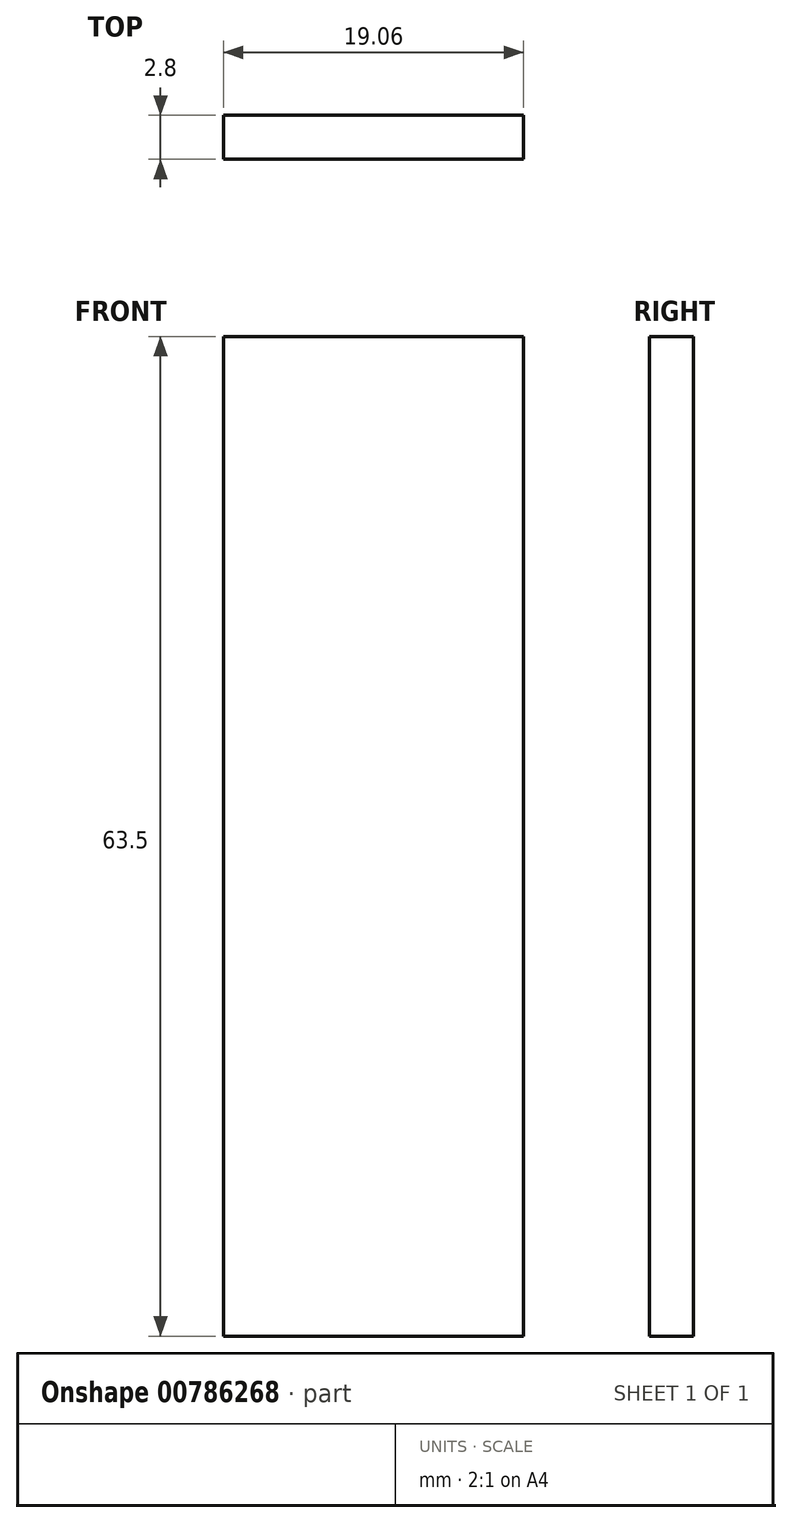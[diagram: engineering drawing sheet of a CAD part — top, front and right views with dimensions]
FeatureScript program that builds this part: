
annotation { "Feature Type Name" : "Feature", "Feature Type Description" : "" }
export const myFeature = defineFeature(function(context is Context, id is Id, definition is map)
    precondition{}
    {
        {
            var Q0;
            Q0=qCreatedBy(makeId("Top.planeOp"),FACE);
            var sketch = newSketch(context, id + "F0", { "sketchPlane" : qUnion([Q0])});
            skLineSegment(sketch, "E0.bottom", {"start": v(9.53, -1.4) * mm, "end": v(-9.53, -1.4) * mm});
            skLineSegment(sketch, "E0.top", {"start": v(9.53, 1.4) * mm, "end": v(-9.53, 1.4) * mm});
            skLineSegment(sketch, "E0.left", {"start": v(9.53, -1.4) * mm, "end": v(9.53, 1.4) * mm});
            skLineSegment(sketch, "E0.right", {"start": v(-9.53, -1.4) * mm, "end": v(-9.53, 1.4) * mm});
            skPoint(sketch, "E0.middle", {"position": v(0, 0) * mm});
            skSolve(sketch);
        }
        {
            var Q0;
            Q0 = qSketchRegion(id + "F0", true);
            extrude(context, id + "F1", {"entities" : qUnion([Q0]), "depth" : 63.5 * mm, "offsetDistance" : 25.4 * mm});
        }
    });
